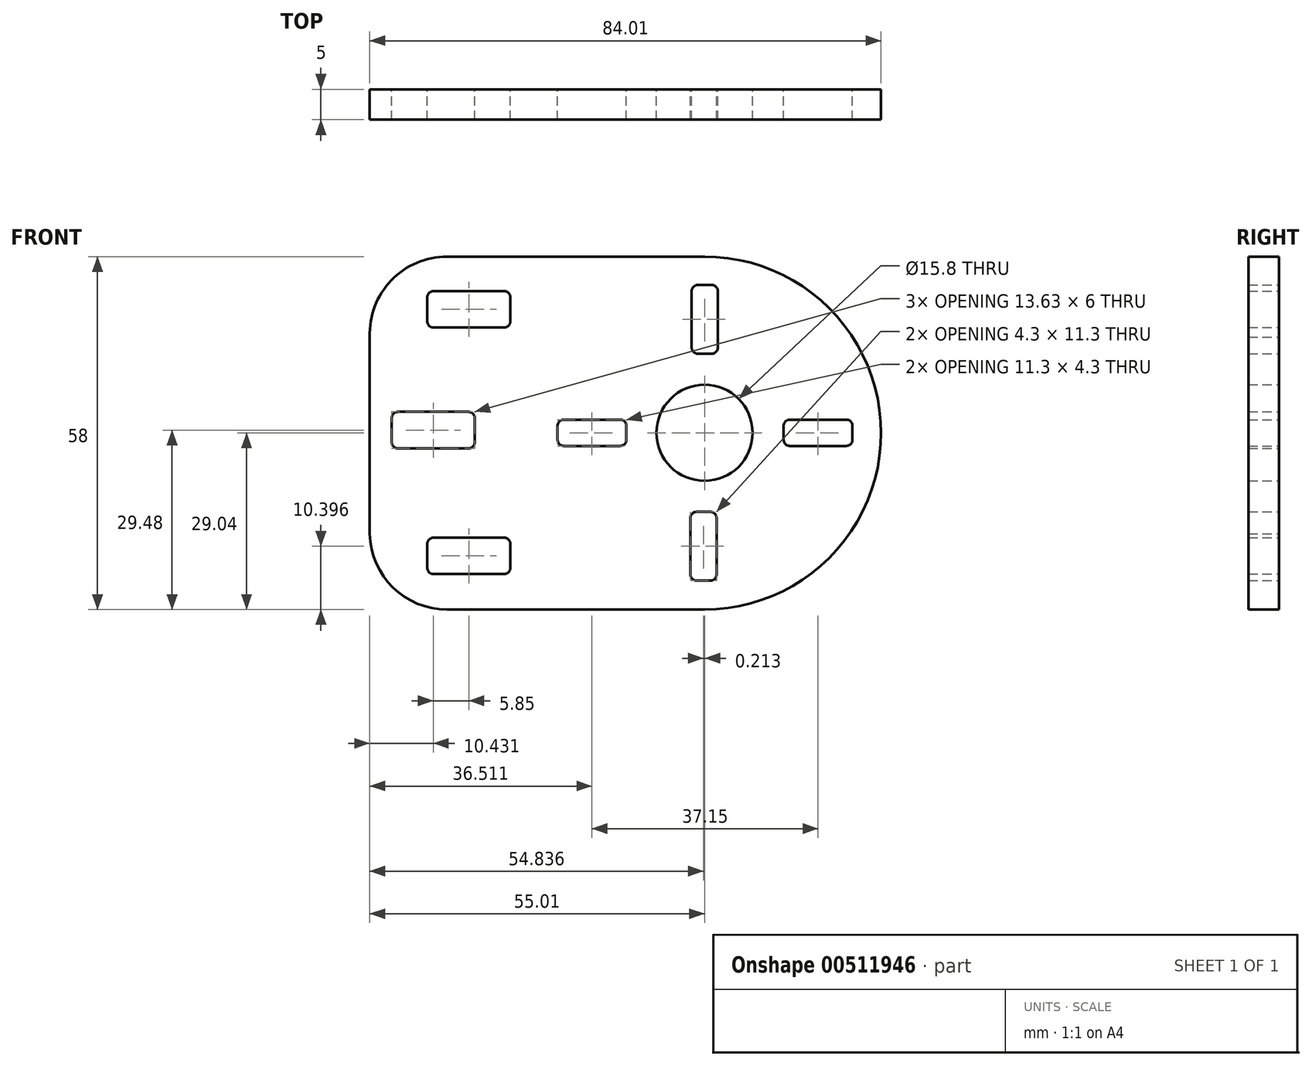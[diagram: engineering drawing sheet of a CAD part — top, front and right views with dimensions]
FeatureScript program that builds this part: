
annotation { "Feature Type Name" : "Feature", "Feature Type Description" : "" }
export const myFeature = defineFeature(function(context is Context, id is Id, definition is map)
    precondition{}
    {
        {
            var Q0;
            Q0=qCreatedBy(makeId("Front.planeOp"),FACE);
            var sketch = newSketch(context, id + "F0", { "sketchPlane" : qUnion([Q0])});
            skLineSegment(sketch, "E0.bottom", {"start": v(-42.3, 28.96) * mm, "end": v(0.04, 28.96) * mm});
            skLineSegment(sketch, "E0.top", {"start": v(-42.3, -29.04) * mm, "end": v(0, -29.04) * mm});
            skCircle(sketch, "E1", {"center": v(0, -0.04) * mm, "radius": 29 * mm});
            skArc(sketch, "E2.filletArc", {"start": v(-42.3, 28.96) * mm, "mid": v(-51.47, 25.05) * mm, "end": v(-55, 15.74) * mm});
            skArc(sketch, "E3.filletArc", {"start": v(-55, -16.57) * mm, "mid": v(-51.2, -25.4) * mm, "end": v(-42.3, -29.04) * mm});
            skCircle(sketch, "E4", {"center": v(0, 0) * mm, "radius": 7.9 * mm});
            skPoint(sketch, "E5", {"position": v(0.04, 7.9) * mm});
            skPoint(sketch, "E6", {"position": v(7.9, 0) * mm});
            skPoint(sketch, "E7", {"position": v(-0.35, -7.9) * mm});
            skPoint(sketch, "E8", {"position": v(-7.9, 0) * mm});
            skLineSegment(sketch, "E9", {"start": v(-0.35, -7.9) * mm, "end": v(0, -29.04) * mm});
            skLineSegment(sketch, "E10", {"start": v(-55, 15.74) * mm, "end": v(-55, -16.57) * mm});
            skPoint(sketch, "E11", {"position": v(-24.15, 0) * mm});
            skPoint(sketch, "E12", {"position": v(-13, 0) * mm});
            skPoint(sketch, "E13", {"position": v(-18.5, 0) * mm});
            skLineSegment(sketch, "E14", {"start": v(-23.15, 2.15) * mm, "end": v(-22, 2.15) * mm});
            skLineSegment(sketch, "E15.top", {"start": v(-23.15, -2.15) * mm, "end": v(-13.85, -2.15) * mm});
            skLineSegment(sketch, "E15.left", {"start": v(-24.15, 1.15) * mm, "end": v(-24.15, -1.15) * mm});
            skLineSegment(sketch, "E15.right", {"start": v(-12.85, 1.15) * mm, "end": v(-12.85, -1.15) * mm});
            skLineSegment(sketch, "E16.bottom", {"start": v(14, 2.15) * mm, "end": v(23.3, 2.15) * mm});
            skLineSegment(sketch, "E16.top", {"start": v(14, -2.15) * mm, "end": v(23.3, -2.15) * mm});
            skLineSegment(sketch, "E16.left", {"start": v(13, 1.15) * mm, "end": v(13, -1.15) * mm});
            skLineSegment(sketch, "E16.right", {"start": v(24.3, 1.15) * mm, "end": v(24.3, -1.15) * mm});
            skPoint(sketch, "E16.middle", {"position": v(18.65, 0) * mm});
            skPoint(sketch, "E17", {"position": v(0.04, 18.65) * mm});
            skLineSegment(sketch, "E18.bottom", {"start": v(1.19, 13) * mm, "end": v(-1.11, 13) * mm});
            skLineSegment(sketch, "E18.top", {"start": v(1.19, 24.3) * mm, "end": v(-1.11, 24.3) * mm});
            skLineSegment(sketch, "E18.left", {"start": v(2.19, 14) * mm, "end": v(2.19, 23.3) * mm});
            skLineSegment(sketch, "E18.right", {"start": v(-2.11, 14) * mm, "end": v(-2.11, 23.3) * mm});
            skLineSegment(sketch, "E19.bottom", {"start": v(-1.32, -13) * mm, "end": v(0.98, -13) * mm});
            skLineSegment(sketch, "E19.top", {"start": v(-1.32, -24.3) * mm, "end": v(0.98, -24.3) * mm});
            skLineSegment(sketch, "E19.left", {"start": v(-2.32, -14) * mm, "end": v(-2.32, -23.3) * mm});
            skLineSegment(sketch, "E19.right", {"start": v(1.98, -14) * mm, "end": v(1.98, -23.3) * mm});
            skPoint(sketch, "E19.middle", {"position": v(-0.17, -18.64) * mm});
            skPoint(sketch, "E20", {"position": v(0, 13) * mm});
            skPoint(sketch, "E21", {"position": v(13, 0) * mm});
            skPoint(sketch, "E22", {"position": v(-0.27, -13) * mm});
            skPoint(sketch, "E23.visualSharp", {"position": v(-2.11, 24.3) * mm});
            skArc(sketch, "E23.filletArc", {"start": v(-1.11, 24.3) * mm, "mid": v(-1.82, 24) * mm, "end": v(-2.11, 23.3) * mm});
            skPoint(sketch, "E24.visualSharp", {"position": v(2.19, 24.3) * mm});
            skArc(sketch, "E24.filletArc", {"start": v(2.19, 23.3) * mm, "mid": v(1.9, 24) * mm, "end": v(1.19, 24.3) * mm});
            skPoint(sketch, "E25.visualSharp", {"position": v(2.19, 13) * mm});
            skArc(sketch, "E25.filletArc", {"start": v(1.19, 13) * mm, "mid": v(1.9, 13.3) * mm, "end": v(2.19, 14) * mm});
            skPoint(sketch, "E26.visualSharp", {"position": v(-2.11, 13) * mm});
            skArc(sketch, "E26.filletArc", {"start": v(-2.11, 14) * mm, "mid": v(-1.82, 13.3) * mm, "end": v(-1.11, 13) * mm});
            skPoint(sketch, "E27.visualSharp", {"position": v(-12.85, 2.15) * mm});
            skArc(sketch, "E27.filletArc", {"start": v(-12.85, 1.15) * mm, "mid": v(-13.14, 1.86) * mm, "end": v(-13.85, 2.15) * mm});
            skPoint(sketch, "E28.visualSharp", {"position": v(-12.85, -2.15) * mm});
            skArc(sketch, "E28.filletArc", {"start": v(-13.85, -2.15) * mm, "mid": v(-13.14, -1.86) * mm, "end": v(-12.85, -1.15) * mm});
            skPoint(sketch, "E29.visualSharp", {"position": v(-24.15, -2.15) * mm});
            skArc(sketch, "E29.filletArc", {"start": v(-24.15, -1.15) * mm, "mid": v(-23.86, -1.86) * mm, "end": v(-23.15, -2.15) * mm});
            skPoint(sketch, "E30.visualSharp", {"position": v(-2.32, -13) * mm});
            skArc(sketch, "E30.filletArc", {"start": v(-1.32, -13) * mm, "mid": v(-2.03, -13.29) * mm, "end": v(-2.32, -14) * mm});
            skPoint(sketch, "E31.visualSharp", {"position": v(1.98, -13) * mm});
            skArc(sketch, "E31.filletArc", {"start": v(1.98, -14) * mm, "mid": v(1.68, -13.29) * mm, "end": v(0.98, -13) * mm});
            skPoint(sketch, "E32.visualSharp", {"position": v(1.98, -24.3) * mm});
            skArc(sketch, "E32.filletArc", {"start": v(0.98, -24.3) * mm, "mid": v(1.68, -24) * mm, "end": v(1.98, -23.3) * mm});
            skPoint(sketch, "E33.visualSharp", {"position": v(-2.32, -24.3) * mm});
            skArc(sketch, "E33.filletArc", {"start": v(-2.32, -23.3) * mm, "mid": v(-2.03, -24) * mm, "end": v(-1.32, -24.3) * mm});
            skPoint(sketch, "E34.visualSharp", {"position": v(13, -2.15) * mm});
            skArc(sketch, "E34.filletArc", {"start": v(13, -1.15) * mm, "mid": v(13.3, -1.86) * mm, "end": v(14, -2.15) * mm});
            skPoint(sketch, "E35.visualSharp", {"position": v(13, 2.15) * mm});
            skArc(sketch, "E35.filletArc", {"start": v(14, 2.15) * mm, "mid": v(13.3, 1.86) * mm, "end": v(13, 1.15) * mm});
            skPoint(sketch, "E36.visualSharp", {"position": v(24.3, 2.15) * mm});
            skArc(sketch, "E36.filletArc", {"start": v(24.3, 1.15) * mm, "mid": v(24, 1.86) * mm, "end": v(23.3, 2.15) * mm});
            skPoint(sketch, "E37.visualSharp", {"position": v(24.3, -2.15) * mm});
            skArc(sketch, "E37.filletArc", {"start": v(23.3, -2.15) * mm, "mid": v(24, -1.86) * mm, "end": v(24.3, -1.15) * mm});
            skLineSegment(sketch, "E38", {"start": v(-38.73, 28.96) * mm, "end": v(-38.73, -29.04) * mm});
            skPoint(sketch, "E39", {"position": v(-41.23, 0.44) * mm});
            skLineSegment(sketch, "E40", {"start": v(-41.23, 0.44) * mm, "end": v(-55, 0.44) * mm});
            skPoint(sketch, "E41", {"position": v(-38.73, 20.3) * mm});
            skPoint(sketch, "E42", {"position": v(-38.73, -20.22) * mm});
            skLineSegment(sketch, "E43.left", {"start": v(-41.23, 3.44) * mm, "end": v(-41.23, -1.32) * mm});
            skLineSegment(sketch, "E44.bottom", {"start": v(-44.55, 23.3) * mm, "end": v(-32.91, 23.3) * mm});
            skLineSegment(sketch, "E44.top", {"start": v(-44.55, 17.3) * mm, "end": v(-32.91, 17.3) * mm});
            skLineSegment(sketch, "E44.left", {"start": v(-45.55, 22.3) * mm, "end": v(-45.55, 18.3) * mm});
            skLineSegment(sketch, "E44.right", {"start": v(-31.91, 22.3) * mm, "end": v(-31.91, 18.3) * mm});
            skLineSegment(sketch, "E45.bottom", {"start": v(-44.55, -17.22) * mm, "end": v(-32.91, -17.22) * mm});
            skLineSegment(sketch, "E45.top", {"start": v(-44.55, -23.22) * mm, "end": v(-32.91, -23.22) * mm});
            skLineSegment(sketch, "E45.left", {"start": v(-45.55, -18.22) * mm, "end": v(-45.55, -22.22) * mm});
            skLineSegment(sketch, "E45.right", {"start": v(-31.91, -18.22) * mm, "end": v(-31.91, -22.22) * mm});
            skPoint(sketch, "E46", {"position": v(-44.58, 0.44) * mm});
            skLineSegment(sketch, "E47.bottom", {"start": v(-50.4, 3.44) * mm, "end": v(-38.76, 3.44) * mm});
            skLineSegment(sketch, "E47.top", {"start": v(-50.4, -2.56) * mm, "end": v(-38.76, -2.56) * mm});
            skLineSegment(sketch, "E47.left", {"start": v(-51.4, 2.44) * mm, "end": v(-51.4, -1.56) * mm});
            skLineSegment(sketch, "E47.right", {"start": v(-37.76, 2.44) * mm, "end": v(-37.76, -1.56) * mm});
            skPoint(sketch, "E48.visualSharp", {"position": v(-24.15, 2.15) * mm});
            skArc(sketch, "E48.filletArc", {"start": v(-23.15, 2.15) * mm, "mid": v(-23.86, 1.86) * mm, "end": v(-24.15, 1.15) * mm});
            skLineSegment(sketch, "E49", {"start": v(-22, 2.15) * mm, "end": v(-13.85, 2.15) * mm});
            skPoint(sketch, "E50.visualSharp", {"position": v(-45.55, 23.3) * mm});
            skArc(sketch, "E50.filletArc", {"start": v(-44.55, 23.3) * mm, "mid": v(-45.25, 23) * mm, "end": v(-45.55, 22.3) * mm});
            skPoint(sketch, "E51.visualSharp", {"position": v(-31.91, 23.3) * mm});
            skArc(sketch, "E51.filletArc", {"start": v(-31.91, 22.3) * mm, "mid": v(-32.2, 23) * mm, "end": v(-32.91, 23.3) * mm});
            skPoint(sketch, "E52.visualSharp", {"position": v(-31.91, 17.3) * mm});
            skArc(sketch, "E52.filletArc", {"start": v(-32.91, 17.3) * mm, "mid": v(-32.2, 17.58) * mm, "end": v(-31.91, 18.3) * mm});
            skPoint(sketch, "E53.visualSharp", {"position": v(-45.55, 17.3) * mm});
            skArc(sketch, "E53.filletArc", {"start": v(-45.55, 18.3) * mm, "mid": v(-45.25, 17.58) * mm, "end": v(-44.55, 17.3) * mm});
            skPoint(sketch, "E54.visualSharp", {"position": v(-37.76, 3.44) * mm});
            skArc(sketch, "E54.filletArc", {"start": v(-37.76, 2.44) * mm, "mid": v(-38.06, 3.15) * mm, "end": v(-38.76, 3.44) * mm});
            skPoint(sketch, "E55.visualSharp", {"position": v(-37.76, -2.56) * mm});
            skArc(sketch, "E55.filletArc", {"start": v(-38.76, -2.56) * mm, "mid": v(-38.06, -2.27) * mm, "end": v(-37.76, -1.56) * mm});
            skPoint(sketch, "E56.visualSharp", {"position": v(-51.4, 3.44) * mm});
            skArc(sketch, "E56.filletArc", {"start": v(-50.4, 3.44) * mm, "mid": v(-51.1, 3.15) * mm, "end": v(-51.4, 2.44) * mm});
            skPoint(sketch, "E57.visualSharp", {"position": v(-51.4, -2.56) * mm});
            skArc(sketch, "E57.filletArc", {"start": v(-51.4, -1.56) * mm, "mid": v(-51.1, -2.27) * mm, "end": v(-50.4, -2.56) * mm});
            skPoint(sketch, "E58.visualSharp", {"position": v(-31.91, -17.22) * mm});
            skArc(sketch, "E58.filletArc", {"start": v(-31.91, -18.22) * mm, "mid": v(-32.2, -17.52) * mm, "end": v(-32.91, -17.22) * mm});
            skPoint(sketch, "E59.visualSharp", {"position": v(-45.55, -23.22) * mm});
            skArc(sketch, "E59.filletArc", {"start": v(-45.55, -22.22) * mm, "mid": v(-45.25, -22.93) * mm, "end": v(-44.55, -23.22) * mm});
            skPoint(sketch, "E60.visualSharp", {"position": v(-45.55, -17.22) * mm});
            skArc(sketch, "E60.filletArc", {"start": v(-44.55, -17.22) * mm, "mid": v(-45.25, -17.52) * mm, "end": v(-45.55, -18.22) * mm});
            skPoint(sketch, "E61.visualSharp", {"position": v(-31.91, -23.22) * mm});
            skArc(sketch, "E61.filletArc", {"start": v(-32.91, -23.22) * mm, "mid": v(-32.2, -22.93) * mm, "end": v(-31.91, -22.22) * mm});
            skSolve(sketch);
        }
        {
            var Q0;
            Q0=qSketchRegion(id+"F0",true);
            extrude(context, id + "F1", {"entities" : qUnion([Q0]), "depth" : 5 * mm});
        }
        {
            var Q0;
            Q0=makeQuery(id+"F1.opExtrude","SWEPT_BODY",BODY,{"disambiguationData":[OSD([sQuery(id+"F0.wireOp",EDGE,"E0.bottom"),sQuery(id+"F0.wireOp",EDGE,"E0.top"),sQuery(id+"F0.wireOp",EDGE,"E1"),sQuery(id+"F0.wireOp",EDGE,"E2.filletArc"),sQuery(id+"F0.wireOp",EDGE,"E3.filletArc"),sQuery(id+"F0.wireOp",EDGE,"E4"),sQuery(id+"F0.wireOp",EDGE,"E10"),sQuery(id+"F0.wireOp",EDGE,"E14"),sQuery(id+"F0.wireOp",EDGE,"E15.top"),sQuery(id+"F0.wireOp",EDGE,"E15.left"),sQuery(id+"F0.wireOp",EDGE,"E15.right"),sQuery(id+"F0.wireOp",EDGE,"E16.bottom"),sQuery(id+"F0.wireOp",EDGE,"E16.top"),sQuery(id+"F0.wireOp",EDGE,"E16.left"),sQuery(id+"F0.wireOp",EDGE,"E16.right"),sQuery(id+"F0.wireOp",EDGE,"E18.bottom"),sQuery(id+"F0.wireOp",EDGE,"E18.top"),sQuery(id+"F0.wireOp",EDGE,"E18.left"),sQuery(id+"F0.wireOp",EDGE,"E18.right"),sQuery(id+"F0.wireOp",EDGE,"E19.bottom"),sQuery(id+"F0.wireOp",EDGE,"E19.top"),sQuery(id+"F0.wireOp",EDGE,"E19.left"),sQuery(id+"F0.wireOp",EDGE,"E19.right"),sQuery(id+"F0.wireOp",EDGE,"E23.filletArc"),sQuery(id+"F0.wireOp",EDGE,"E24.filletArc"),sQuery(id+"F0.wireOp",EDGE,"E25.filletArc"),sQuery(id+"F0.wireOp",EDGE,"E26.filletArc"),sQuery(id+"F0.wireOp",EDGE,"E27.filletArc"),sQuery(id+"F0.wireOp",EDGE,"E28.filletArc"),sQuery(id+"F0.wireOp",EDGE,"E29.filletArc"),sQuery(id+"F0.wireOp",EDGE,"E30.filletArc"),sQuery(id+"F0.wireOp",EDGE,"E31.filletArc"),sQuery(id+"F0.wireOp",EDGE,"E32.filletArc"),sQuery(id+"F0.wireOp",EDGE,"E33.filletArc"),sQuery(id+"F0.wireOp",EDGE,"E34.filletArc"),sQuery(id+"F0.wireOp",EDGE,"E35.filletArc"),sQuery(id+"F0.wireOp",EDGE,"E36.filletArc"),sQuery(id+"F0.wireOp",EDGE,"E37.filletArc"),sQuery(id+"F0.wireOp",EDGE,"E44.bottom"),sQuery(id+"F0.wireOp",EDGE,"E44.top"),sQuery(id+"F0.wireOp",EDGE,"E44.left"),sQuery(id+"F0.wireOp",EDGE,"E44.right"),sQuery(id+"F0.wireOp",EDGE,"E45.bottom"),sQuery(id+"F0.wireOp",EDGE,"E45.top"),sQuery(id+"F0.wireOp",EDGE,"E45.left"),sQuery(id+"F0.wireOp",EDGE,"E45.right"),sQuery(id+"F0.wireOp",EDGE,"E47.bottom"),sQuery(id+"F0.wireOp",EDGE,"E47.top"),sQuery(id+"F0.wireOp",EDGE,"E47.left"),sQuery(id+"F0.wireOp",EDGE,"E47.right"),sQuery(id+"F0.wireOp",EDGE,"E48.filletArc"),sQuery(id+"F0.wireOp",EDGE,"E49"),sQuery(id+"F0.wireOp",EDGE,"E50.filletArc"),sQuery(id+"F0.wireOp",EDGE,"E51.filletArc"),sQuery(id+"F0.wireOp",EDGE,"E52.filletArc"),sQuery(id+"F0.wireOp",EDGE,"E53.filletArc"),sQuery(id+"F0.wireOp",EDGE,"E54.filletArc"),sQuery(id+"F0.wireOp",EDGE,"E55.filletArc"),sQuery(id+"F0.wireOp",EDGE,"E56.filletArc"),sQuery(id+"F0.wireOp",EDGE,"E57.filletArc"),sQuery(id+"F0.wireOp",EDGE,"E58.filletArc"),sQuery(id+"F0.wireOp",EDGE,"E59.filletArc"),sQuery(id+"F0.wireOp",EDGE,"E60.filletArc"),sQuery(id+"F0.wireOp",EDGE,"E61.filletArc")])]});
            transform(context, id + "F2", {"entities" : qUnion([Q0]), "transformType" : TransformType.TRANSLATION_3D, "dx" : 0 * mm, "dy" : 0 * mm, "dz" : 0 * mm, "makeCopy" : false});
        }
    });
